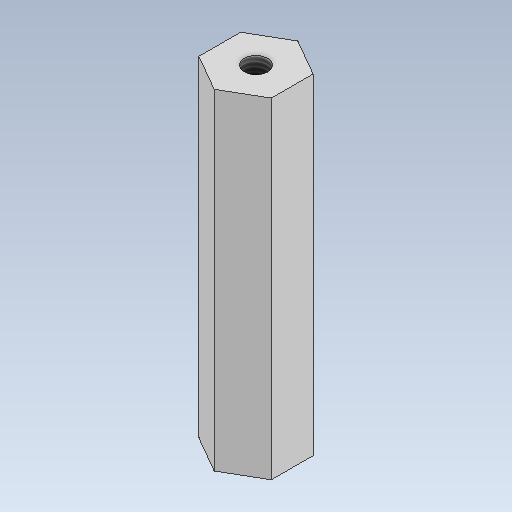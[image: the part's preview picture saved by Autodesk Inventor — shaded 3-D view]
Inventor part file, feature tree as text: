
AUTODESK INVENTOR PART (.ipt)
format: ipt  version: 2023 (Build 270158000, 158)  size: 95,744 bytes
history: native  units: in
note: dims shown in document units (in); Inventor stores cm internally (conversion verified against a paired STEP export)
features: other x3, sketch x3
ambient origin geometry x8: Origin, YZ Plane, XZ Plane, XY Plane, X Axis, Y Axis, Z Axis, Center Point
bodies: Solid1 (feature_tree)
feature tree (6):
  other  "HexShaft.ipt"
  other  "Solid1::HexShaft.ipt"
  other  "TaggingFeature1"
  sketch  "Sketch1"  dims[d0=0.3937in]
  sketch  "Sketch3"
  sketch  "Sketch4"
